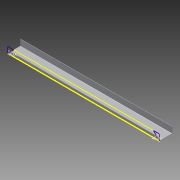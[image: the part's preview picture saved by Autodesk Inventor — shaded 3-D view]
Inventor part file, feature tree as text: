
AUTODESK INVENTOR PART (.ipt)
format: ipt  version: 2013 (Build 170138000, 138)  size: 142,848 bytes
history: native  units: in
note: dims shown in document units (in); Inventor stores cm internally (conversion verified against a paired STEP export)
features: sheet_metal_op x7, other x4, projected_geometry x3, sketch x2
ambient origin geometry x8: Origin, YZ Plane, XZ Plane, XY Plane, X Axis, Y Axis, Z Axis, Center Point
bodies: Solid1 (feature_tree)
feature tree (16):
  sheet_metal_op  "Face1"
  sheet_metal_op  "Flange1"
  sheet_metal_op  "Flange2"
  sketch  "Sketch5"  dims[d1=4.0in d2=0.0938in d3=0.0938in d4=0.0469in d5=0.1875in d6=0.0938in d7=2.0in d8=90.0deg d9=0.0938in d10=0.375in d11=0.0938in d12=0.0938in d13=0.0938in d14=0.0469in d15=0.1875in d16=0.0938in d17=1.0in d18=90.0deg d19=0.0938in d20=0.375in d21=0.0938in d22=0.0938in d39=45.0deg d40=45.0deg]
  sketch  "Sketch1"  dims[d0=48.0in]
  other  "Plate1"
  other  "Plate2"
  sheet_metal_op  "Bend1"
  sheet_metal_op  "Corner1"
  other  "Plate3"
  sheet_metal_op  "Bend2"
  sheet_metal_op  "Corner2"
  projected_geometry  "Projected Loop1"
  projected_geometry  "Projected Loop2"
  projected_geometry  "Projected Loop3"
  other  "Definition1"
